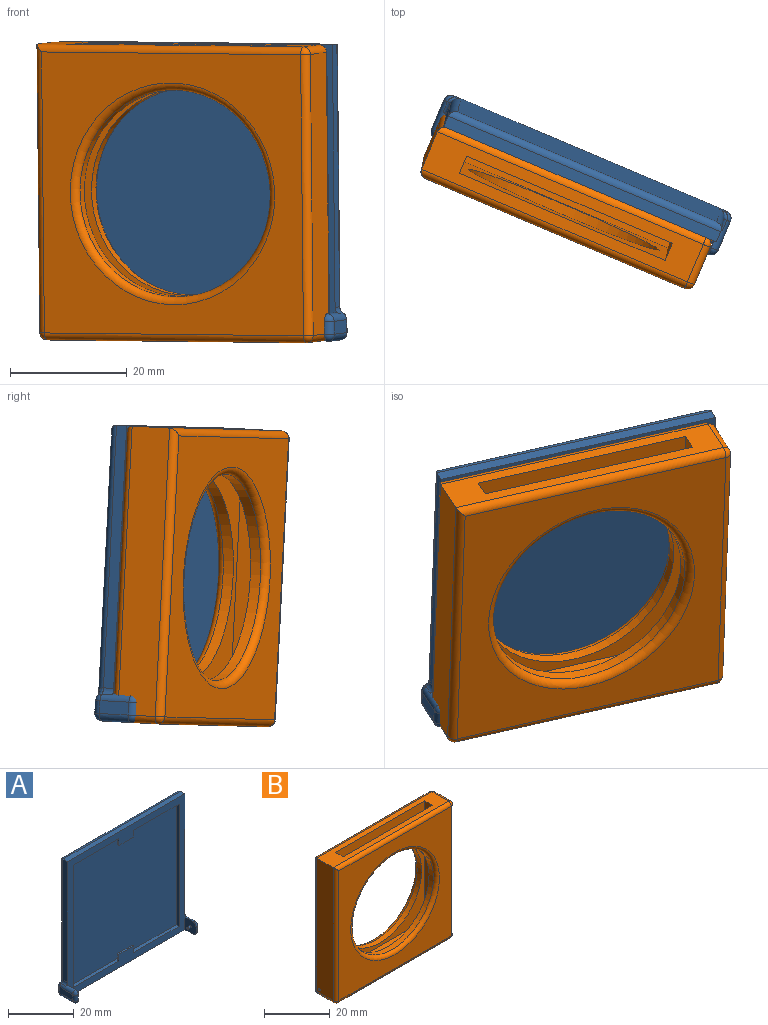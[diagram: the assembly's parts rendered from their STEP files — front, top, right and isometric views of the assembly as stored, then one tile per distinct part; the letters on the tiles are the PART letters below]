
ASSEMBLY  parts=2 mates=1
PART A: 53 faces, bbox 53.3x7.9x50.8 mm
  f0: plane 45.11x1.91mm, normal (1,0,0), area 85.9mm2, adj f2,f4,f33,f42
  f1: plane 45.11x1.91mm, normal (-1,0,0), area 85.9mm2, adj f2,f4,f29,f51
  f2: plane 52.07x50.8mm, normal (0,-1,0), area 522.8mm2, adj f0,f1,f3,f4,f6,f7,f8,f9
  f3: plane 50.8x1.91mm, normal (0,0,-1), area 96.8mm2, adj f2,f30,f40,f49
  f4: plane 50.8x1.91mm, normal (0,0,1), area 96.8mm2, adj f0,f1,f2,f31
  f5: plane 50.8x48.26mm, normal (0,1,0), area 2334.7mm2, adj f27,f28,f29,f30,f31,f32,f33,f34
  f6: plane 45.72x1.27mm, normal (1,0,0), area 58.1mm2, adj f2,f7,f9,f10
  f7: plane 45.72x1.27mm, normal (0,0,1), area 54.8mm2, adj f2,f6,f8,f10,f11,f12,f13
  f8: plane 45.72x1.27mm, normal (-1,0,0), area 58.1mm2, adj f2,f7,f9,f10
  f9: plane 45.72x1.27mm, normal (0,0,-1), area 54mm2, adj f2,f6,f8,f10,f15,f16,f17
  f10: plane 45.72x45.72mm, normal (0,-1,0), area 2090.3mm2, adj f6,f7,f8,f9
  f11: plane 6.35x2.54mm, normal (0,1,0), area 16.1mm2, adj f7,f12,f13,f14
  f12: plane 2.54x0.51mm, normal (-1,0,0), area 1.3mm2, adj f2,f7,f11,f14
  f13: plane 2.54x0.51mm, normal (1,0,0), area 1.3mm2, adj f2,f7,f11,f14
  f14: plane 6.35x0.51mm, normal (0,0,1), area 3.2mm2, adj f2,f11,f12,f13
  f15: plane 6.35x2.54mm, normal (0,1,0), area 16.1mm2, adj f9,f16,f17,f18
  f16: plane 2.54x0.64mm, normal (-1,0,0), area 1.6mm2, adj f2,f9,f15,f18
  f17: plane 2.54x0.64mm, normal (1,0,0), area 1.6mm2, adj f2,f9,f15,f18
  f18: plane 6.35x0.64mm, normal (0,0,-1), area 4mm2, adj f2,f15,f16,f17
  f19: plane 4.76x4.76mm, normal (1,0,0), area 21.7mm2, adj f2,f21,f45,f46,f47,f48,f49
  f20: plane 5.4x2.22mm, normal (-1,0,0), area 12mm2, adj f28,f45,f47,f49
  f21: cylinder r=0.32mm len=1.27mm, axis (-1,0,0), area 2.5mm2, adj f19,f22
  f22: plane 0.64x0.64mm, normal (1,0,0), area 0.3mm2, adj f21
  f23: plane 5.4x2.22mm, normal (1,0,0), area 12mm2, adj f32,f36,f38,f40
  f24: plane 4.76x4.76mm, normal (-1,0,0), area 21.7mm2, adj f2,f25,f36,f37,f38,f39,f40
  f25: cylinder r=0.32mm len=1.27mm, axis (1,0,0), area 2.5mm2, adj f24,f26
  f26: plane 0.64x0.64mm, normal (-1,0,0), area 0.3mm2, adj f25
  f27: cylinder r=1.27mm len=1.27mm, axis (-1,0,0), area 0.5mm2, adj f5,f29,f44,f52
  f28: cylinder r=1.27mm len=2.22mm, axis (0,0,-1), area 4.4mm2, adj f5,f20,f44,f50
  f29: cylinder r=1.27mm len=47.31mm, axis (0,0,-1), area 90.6mm2, adj f1,f5,f27,f31,f52
  f30: cylinder r=1.27mm len=50.8mm, axis (1,0,0), area 101.3mm2, adj f3,f5,f41,f50
  f31: cylinder r=1.27mm len=50.8mm, axis (-1,0,0), area 98.8mm2, adj f4,f5,f29,f33
  f32: cylinder r=1.27mm len=2.22mm, axis (0,0,-1), area 4.4mm2, adj f5,f23,f35,f41
  f33: cylinder r=1.27mm len=47.31mm, axis (0,0,1), area 90.6mm2, adj f0,f5,f31,f34,f43
  f34: cylinder r=1.27mm len=1.27mm, axis (-1,0,0), area 0.5mm2, adj f5,f33,f35,f43
  f35: sphere r=1.27mm, area 2mm2, adj f32,f34,f36,f43
  f36: cylinder r=1.27mm len=5.4mm, axis (0,1,0), area 9.5mm2, adj f2,f23,f24,f35,f37,f42
  f37: sphere r=1.27mm, area 2.5mm2, adj f24,f36,f38
  f38: cylinder r=1.27mm len=2.22mm, axis (0,0,1), area 4.4mm2, adj f23,f24,f37,f39
  f39: sphere r=1.27mm, area 2.5mm2, adj f24,f38,f40
  f40: cylinder r=1.27mm len=5.4mm, axis (0,1,0), area 10.8mm2, adj f3,f23,f24,f39,f41
  f41: sphere r=1.27mm, area 2.5mm2, adj f30,f32,f40
  f42: cylinder r=1.27mm len=1.91mm, axis (0,1,0), area 2.5mm2, adj f0,f2,f36,f43
  f43: bspline ~2.15x1.59mm, area 2mm2, adj f33,f34,f35,f42
  f44: sphere r=1.27mm, area 1.8mm2, adj f27,f28,f45,f52
  f45: cylinder r=1.27mm len=5.4mm, axis (0,-1,0), area 9.5mm2, adj f2,f19,f20,f44,f46,f51
  f46: sphere r=1.27mm, area 2.5mm2, adj f19,f45,f47
  f47: cylinder r=1.27mm len=2.22mm, axis (0,0,-1), area 4.4mm2, adj f19,f20,f46,f48
  f48: sphere r=1.27mm, area 2.5mm2, adj f19,f47,f49
  f49: cylinder r=1.27mm len=5.4mm, axis (0,1,0), area 10.8mm2, adj f3,f19,f20,f48,f50
  f50: sphere r=1.27mm, area 3.5mm2, adj f28,f30,f49
  f51: cylinder r=1.27mm len=1.91mm, axis (0,-1,0), area 2.5mm2, adj f1,f2,f45,f52
  f52: bspline ~2.15x1.59mm, area 2mm2, adj f27,f29,f44,f51
PART B: 36 faces, bbox 50.8x9.5x50.8 mm
  f0: plane 49.53x6.99mm, normal (0,0,1), area 223.2mm2, adj f2,f8,f9,f10,f11,f17,f20,f30
  f1: cylinder r=17.78mm len=35.56mm, axis (0,-1,0), area 211.4mm2, adj f8,f13
  f2: plane 49.53x6.99mm, normal (-1,0,0), area 345.7mm2, adj f0,f15,f19,f27,f34
  f3: plane 48.26x6.99mm, normal (0,0,-1), area 337.1mm2, adj f16,f23,f25,f27
  f4: plane 48.26x6.99mm, normal (1,0,0), area 336.8mm2, adj f18,f21,f23,f30,f32
  f5: plane 48.26x48.26mm, normal (0,-1,0), area 1188.9mm2, adj f14,f19,f20,f21,f25
  f6: plane 48.26x48.26mm, normal (0,1,0), area 1188.9mm2, adj f13,f15,f16,f17,f18
  f7: cylinder r=17.78mm len=35.56mm, axis (0,-1,0), area 211.4mm2, adj f9,f14
  f8: plane 44.45x38.35mm, normal (0,-1,0), area 711.7mm2, adj f0,f1,f10,f11,f12
  f9: plane 44.45x38.35mm, normal (0,1,0), area 711.7mm2, adj f0,f7,f10,f11,f12
  f10: plane 44.45x3.2mm, normal (1,0,0), area 142.3mm2, adj f0,f8,f9,f12
  f11: plane 44.45x3.2mm, normal (-1,0,0), area 142.3mm2, adj f0,f8,f9,f12
  f12: plane 38.35x3.2mm, normal (0,0,1), area 122.7mm2, adj f8,f9,f10,f11
  f13: torus R=19.05mm, axis (0,-1,0), area 228.6mm2, adj f1,f6
  f14: torus R=19.05mm, axis (0,-1,0), area 228.6mm2, adj f5,f7
  f15: cylinder r=1.27mm len=49.53mm, axis (0,0,-1), area 97.9mm2, adj f2,f6,f17,f28
  f16: cylinder r=1.27mm len=48.26mm, axis (1,0,0), area 96.3mm2, adj f3,f6,f22,f28
  f17: cylinder r=1.27mm len=49.53mm, axis (-1,0,0), area 97.9mm2, adj f0,f6,f15,f29
  f18: cylinder r=1.27mm len=48.26mm, axis (0,0,1), area 96.3mm2, adj f4,f6,f22,f29
  f19: cylinder r=1.27mm len=49.53mm, axis (0,0,1), area 97.9mm2, adj f2,f5,f20,f26
  f20: cylinder r=1.27mm len=49.53mm, axis (1,0,0), area 97.9mm2, adj f0,f5,f19,f31
  f21: cylinder r=1.27mm len=48.26mm, axis (0,0,-1), area 96.3mm2, adj f4,f5,f24,f31
  f22: sphere r=1.27mm, area 2.5mm2, adj f16,f18,f23
  f23: cylinder r=1.27mm len=6.99mm, axis (0,1,0), area 13.9mm2, adj f3,f4,f22,f24
  f24: sphere r=1.27mm, area 2.5mm2, adj f21,f23,f25
  f25: cylinder r=1.27mm len=48.26mm, axis (-1,0,0), area 96.3mm2, adj f3,f5,f24,f26
  f26: sphere r=1.27mm, area 2.5mm2, adj f19,f25,f27
  f27: cylinder r=1.27mm len=6.99mm, axis (0,-1,0), area 13.9mm2, adj f2,f3,f26,f28
  f28: sphere r=1.27mm, area 2.5mm2, adj f15,f16,f27
  f29: sphere r=1.27mm, area 2.5mm2, adj f17,f18,f30
  f30: cylinder r=1.27mm len=6.99mm, axis (0,-1,0), area 13.9mm2, adj f0,f4,f29,f31
  f31: sphere r=1.27mm, area 2.5mm2, adj f20,f21,f30
  f32: cylinder r=0.32mm len=1.65mm, axis (1,0,0), area 3.3mm2, adj f4,f33
  f33: plane 0.64x0.64mm, normal (1,0,0), area 0.3mm2, adj f32
  f34: cylinder r=0.32mm len=1.65mm, axis (-1,0,0), area 3.3mm2, adj f2,f35
  f35: plane 0.64x0.64mm, normal (-1,0,0), area 0.3mm2, adj f34
PLACE A rot(axis=(0.13,0,-0.99),23.1deg) t=(19.48,26.29,-8.58)mm
PLACE B rot(axis=(0.13,0,-0.99),23.1deg) t=(17.65,23.62,-8.73)mm
MATE revolute B.f32 <-> A.f21  axis (0.92,-0.39,-0.01) through (63.48,1.5,-6.98)mm
